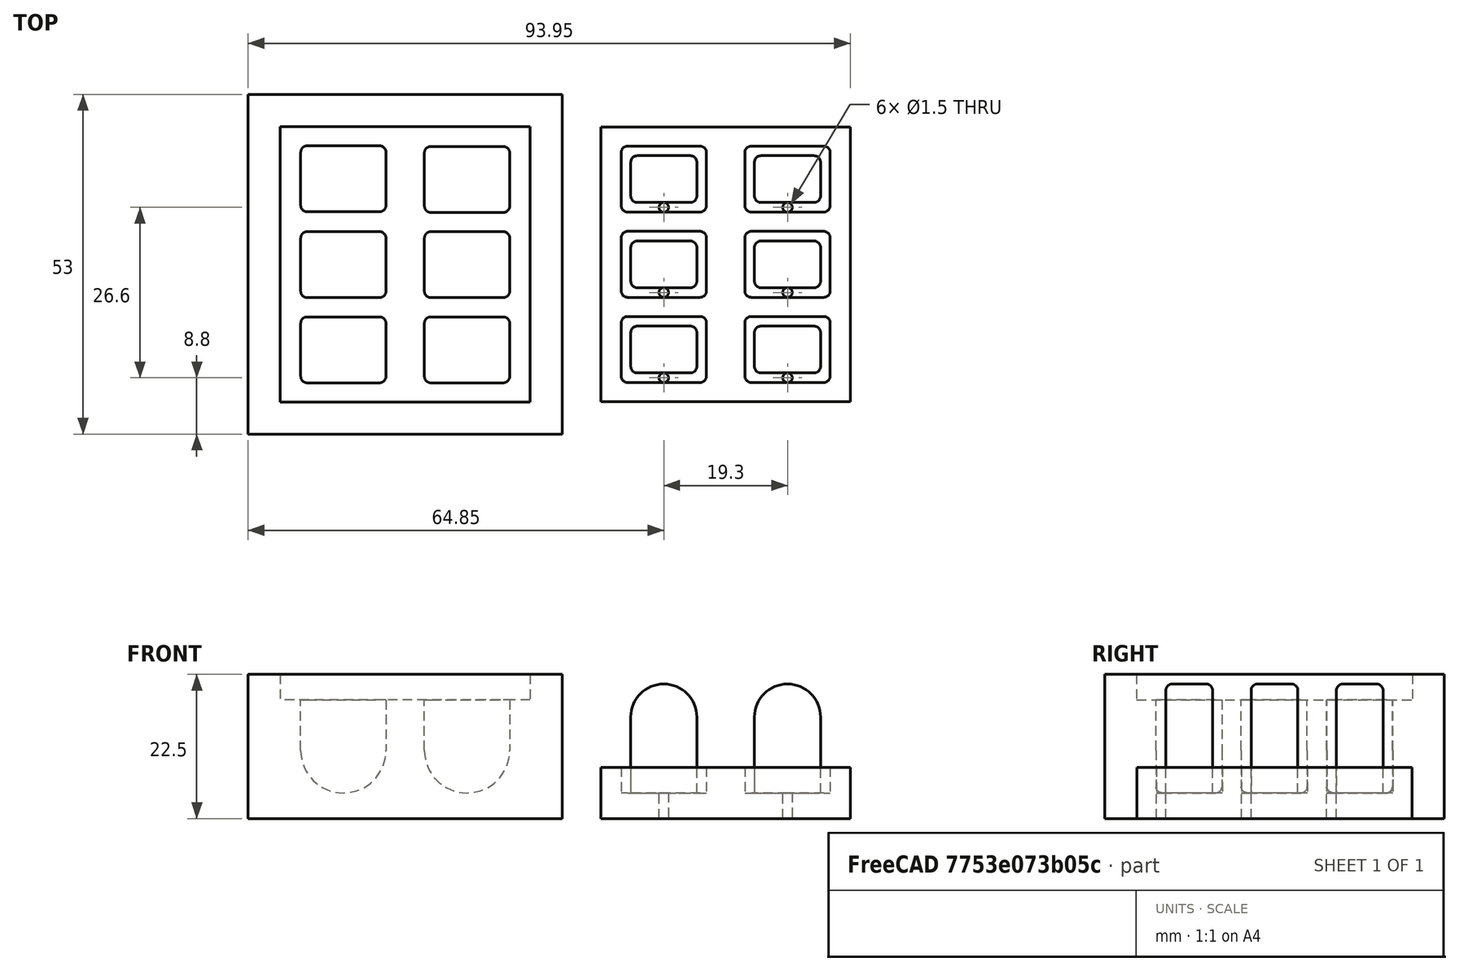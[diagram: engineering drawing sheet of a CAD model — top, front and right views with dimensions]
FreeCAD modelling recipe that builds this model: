
FCSTD DOCUMENT  (FreeCAD 0.21R33771 (Git))
Label: endcap_v3
License: All rights reserved
LicenseURL: http://en.wikipedia.org/wiki/All_rights_reserved
objects: Part::FeaturePython×12, Sketcher::SketchObject×9, Part::Cut×6, PartDesign::Pocket×5, Part::MultiFuse×5, PartDesign::Pad×4, PartDesign::Body×4, PartDesign::LinearPattern×4, Mesh::Feature×3, PartDesign::Fillet×2, Part::Fuse×1
note: 63 computed .brp shape members not serialized (recipe doc carries the construction recipe); baked Part::Feature solids carry a one-line shape summary decoded from their .brp

FEATURE [Sketcher::SketchObject] Sketch
  FullyConstrained = true
  MapMode = 5
  Support = -> [XY_Plane]
  sketch-geometry (5):
    g0: LineSegment StartX=24.5 StartY=-26.5 StartZ=0 EndX=24.5 EndY=26.5 EndZ=0
    g1: LineSegment StartX=24.5 StartY=26.5 StartZ=0 EndX=-24.5 EndY=26.5 EndZ=0
    g2: LineSegment StartX=-24.5 StartY=26.5 StartZ=0 EndX=-24.5 EndY=-26.5 EndZ=0
    g3: LineSegment StartX=-24.5 StartY=-26.5 StartZ=0 EndX=24.5 EndY=-26.5 EndZ=0
    g4: GeomPoint X=0 Y=0 Z=0
  constraints (12):
    c: Coincident(g0,g1)
    c: Coincident(g1,g2)
    c: Coincident(g2,g3)
    c: Coincident(g3,g0)
    c: Horizontal(g1)
    c: Horizontal(g3)
    c: Vertical(g0)
    c: Vertical(g2)
    c: Symmetric(g1,g0,g4)
    c: Coincident(g4,g-1)
    c: Distance(g1) = 49
    c: Distance(g2) = 53
FEATURE [PartDesign::Pad] Pad
  Direction = (0,0,1)
  Length = 22.5
  Length2 = 10
  Profile = -> Sketch
  ReferenceAxis = -> Sketch [N_Axis]
  Type = 0
  expr: Length = 14.5 + 4 + 4
FEATURE [Sketcher::SketchObject] Sketch001
  FullyConstrained = true
  MapMode = 5
  Placement = pos=(0,0,22.5) rot=(0,0,1;0rad)
  Support = -> [Pad]
  sketch-geometry (5):
    g0: LineSegment StartX=19.5 StartY=-21.5 StartZ=0 EndX=19.5 EndY=21.5 EndZ=0
    g1: LineSegment StartX=19.5 StartY=21.5 StartZ=0 EndX=-19.5 EndY=21.5 EndZ=0
    g2: LineSegment StartX=-19.5 StartY=21.5 StartZ=0 EndX=-19.5 EndY=-21.5 EndZ=0
    g3: LineSegment StartX=-19.5 StartY=-21.5 StartZ=0 EndX=19.5 EndY=-21.5 EndZ=0
    g4: GeomPoint X=0 Y=0 Z=0
  constraints (12):
    c: Coincident(g0,g1)
    c: Coincident(g1,g2)
    c: Coincident(g2,g3)
    c: Coincident(g3,g0)
    c: Horizontal(g1)
    c: Horizontal(g3)
    c: Vertical(g0)
    c: Vertical(g2)
    c: Symmetric(g1,g0,g4)
    c: Coincident(g4,g-1)
    c: Distance(g1) = 39
    c: Distance(g2) = 43
FEATURE [PartDesign::Pocket] Pocket
  BaseFeature = -> Pad
  Direction = (0,0,-1)
  Length = 4
  Length2 = 5
  Profile = -> Sketch001
  ReferenceAxis = -> Sketch001 [N_Axis]
  Type = 0
FEATURE [PartDesign::Body] Body  label="base"
  Group = -> [Sketch,Pad,Sketch001,Pocket]
  Origin = -> Origin
  Tip = -> Pocket
FEATURE [Sketcher::SketchObject] Sketch002
  FullyConstrained = true
  MapMode = 5
  Placement = pos=(0,0,0) rot=(1,0,0;1.5708rad)
  Support = -> [XZ_Plane001]
  sketch-geometry (4):
    g0: LineSegment StartX=-6.65 StartY=0 StartZ=0 EndX=6.65 EndY=0 EndZ=0
    g1: LineSegment StartX=6.65 StartY=0 StartZ=0 EndX=6.65 EndY=-7.85 EndZ=0
    g2: ArcOfCircle CenterX=-2.765e-13 CenterY=-7.85 CenterZ=0 NormalX=0 NormalY=0 NormalZ=1 AngleXU=0 Radius=6.65 StartAngle=3.14159 EndAngle=6.28319
    g3: LineSegment StartX=-6.65 StartY=-7.85 StartZ=0 EndX=-6.65 EndY=0 EndZ=0
  constraints (10):
    c: PointOnObject(g0,g-1)
    c: Coincident(g0,g1)
    c: Vertical(g1)
    c: Tangent(g1,g2) = 1.5708
    c: Tangent(g2,g3) = 1.5708
    c: Coincident(g3,g0)
    c: Diameter(g2) = 13.3
    c: Distance(g3) = 7.85
    c: Distance(g0) = 13.3
    c: Symmetric(g0,g0,g-2)
FEATURE [PartDesign::Pad] Pad001
  Direction = (0,-1,2e-16)
  Length = 10.3
  Length2 = 10
  Placement = pos=(0,0,0) rot=(1,0,0;1.5708rad)
  Profile = -> Sketch002
  ReferenceAxis = -> Sketch002 [N_Axis]
  Type = 0
FEATURE [PartDesign::Fillet] Fillet
  Base = -> Pad001 [Edge12,Edge10,Edge7,Edge11,Edge6,Edge9]
  BaseFeature = -> Pad001
  Placement = pos=(0,0,0) rot=(1,0,0;1.5708rad)
  Radius = 1
  SupportTransform = false
  UseAllEdges = false
FEATURE [PartDesign::Body] Body001  label="cup_mother"
  Group = -> [Sketch002,Pad001,Fillet]
  Origin = -> Origin001
  Placement = pos=(9.65,16.95,18.5) rot=(0,0,1;0rad)
  Tip = -> Fillet
FEATURE [Part::FeaturePython] Clone  label="cup001"  # Draft clone (typed FeaturePython)
  AttacherType = Attacher::AttachEngine3D
  Fuse = false
  Objects = -> [Body001]
  Placement = pos=(9.65,18.4,18.5) rot=(0,0,1;0rad)
  Scale = (1,1,1)
FEATURE [Part::FeaturePython] Clone001  label="cup002"  # Draft clone (typed FeaturePython)
  AttacherType = Attacher::AttachEngine3D
  Fuse = false
  Objects = -> [Clone]
  Placement = pos=(9.65,5.1,18.5) rot=(0,0,1;0rad)
  Scale = (1,1,1)
FEATURE [Part::FeaturePython] Clone002  label="cup003"  # Draft clone (typed FeaturePython)
  AttacherType = Attacher::AttachEngine3D
  Fuse = false
  Objects = -> [Clone001]
  Placement = pos=(9.65,-8.2,18.5) rot=(0,0,1;0rad)
  Scale = (1,1,1)
FEATURE [Part::FeaturePython] Clone003  label="cup004"  # Draft clone (typed FeaturePython)
  AttacherType = Attacher::AttachEngine3D
  Fuse = false
  Objects = -> [Clone002]
  Placement = pos=(-9.65,18.5,18.5) rot=(0,0,1;0rad)
  Scale = (1,1,1)
FEATURE [Part::FeaturePython] Clone004  label="cup005"  # Draft clone (typed FeaturePython)
  AttacherType = Attacher::AttachEngine3D
  Fuse = false
  Objects = -> [Clone003]
  Placement = pos=(-9.65,5.1,18.5) rot=(0,0,1;0rad)
  Scale = (1,1,1)
FEATURE [Part::FeaturePython] Clone005  label="cup006"  # Draft clone (typed FeaturePython)
  AttacherType = Attacher::AttachEngine3D
  Fuse = false
  Objects = -> [Clone004]
  Placement = pos=(-9.65,-8.2,18.5) rot=(0,0,1;0rad)
  Scale = (1,1,1)
FEATURE [Sketcher::SketchObject] Sketch003
  FullyConstrained = true
  MapMode = 5
  Support = -> [XY_Plane002]
  sketch-geometry (5):
    g0: LineSegment StartX=19.45 StartY=-21.45 StartZ=0 EndX=19.45 EndY=21.45 EndZ=0
    g1: LineSegment StartX=19.45 StartY=21.45 StartZ=0 EndX=-19.45 EndY=21.45 EndZ=0
    g2: LineSegment StartX=-19.45 StartY=21.45 StartZ=0 EndX=-19.45 EndY=-21.45 EndZ=0
    g3: LineSegment StartX=-19.45 StartY=-21.45 StartZ=0 EndX=19.45 EndY=-21.45 EndZ=0
    g4: GeomPoint X=0 Y=0 Z=0
  constraints (12):
    c: Coincident(g0,g1)
    c: Coincident(g1,g2)
    c: Coincident(g2,g3)
    c: Coincident(g3,g0)
    c: Horizontal(g1)
    c: Horizontal(g3)
    c: Vertical(g0)
    c: Vertical(g2)
    c: Symmetric(g1,g0,g4)
    c: Coincident(g4,g-1)
    c: Distance(g1) = 38.9
    c: Distance(g2) = 42.9
FEATURE [PartDesign::Pad] Pad002
  Direction = (0,0,1)
  Length = 8
  Length2 = 10
  Profile = -> Sketch003
  ReferenceAxis = -> Sketch003 [N_Axis]
  Type = 0
FEATURE [Sketcher::SketchObject] Sketch004  label="overflow001"
  FullyConstrained = true
  MapMode = 5
  Placement = pos=(0,0,8) rot=(0,0,1;0rad)
  Support = -> [Pad002]
  expr: Constraints[16] = 13.3 / 2
  expr: Constraints[20] = 10.3 / 2
  expr: Constraints[21] = 10.3 / 2
  sketch-geometry (9):
    g0: LineSegment StartX=-16.3 StartY=-9.15 StartZ=0 EndX=-16.3 EndY=-17.45 EndZ=0
    g1: LineSegment StartX=-15.3 StartY=-18.45 StartZ=0 EndX=-4 EndY=-18.45 EndZ=0
    g2: LineSegment StartX=-3 StartY=-17.45 StartZ=0 EndX=-3 EndY=-9.15 EndZ=0
    g3: LineSegment StartX=-4 StartY=-8.15 StartZ=0 EndX=-15.3 EndY=-8.15 EndZ=0
    g4: ArcOfCircle CenterX=-4 CenterY=-9.15 CenterZ=0 NormalX=0 NormalY=0 NormalZ=1 AngleXU=0 Radius=1 StartAngle=0 EndAngle=1.5708
    g5: ArcOfCircle CenterX=-15.3 CenterY=-9.15 CenterZ=0 NormalX=0 NormalY=0 NormalZ=1 AngleXU=0 Radius=1 StartAngle=1.5708 EndAngle=3.14159
    g6: ArcOfCircle CenterX=-15.3 CenterY=-17.45 CenterZ=0 NormalX=0 NormalY=0 NormalZ=1 AngleXU=0 Radius=1 StartAngle=3.14159 EndAngle=4.71239
    g7: ArcOfCircle CenterX=-4 CenterY=-17.45 CenterZ=0 NormalX=0 NormalY=0 NormalZ=1 AngleXU=0 Radius=1 StartAngle=4.71239 EndAngle=6.28319
    g8: GeomPoint X=-9.65 Y=-13.3 Z=0
  constraints (22):
    c: Horizontal(g1)
    c: Horizontal(g3)
    c: Vertical(g0)
    c: Vertical(g2)
    c: Tangent(g3,g4) = -1.5708
    c: Tangent(g2,g4) = -1.5708
    c: Tangent(g0,g5) = -1.5708
    c: Tangent(g3,g5) = -1.5708
    c: Tangent(g0,g6) = -1.5708
    c: Tangent(g1,g6) = -1.5708
    c: Tangent(g2,g7) = -1.5708
    c: Tangent(g1,g7) = -1.5708
    c: Radius(g4) = 1
    c: Radius(g7) = 1
    c: Radius(g5) = 1
    c: Radius(g6) = 1
    c: DistanceX(g8,g2) = 6.65
    c: DistanceX(g0,g8) = 6.65
    c: DistanceX(g8,g-1) = 9.65
    c: DistanceY(g8,g-1) = 13.3
    c: DistanceY(g1,g8) = 5.15
    c: DistanceY(g8,g3) = 5.15
FEATURE [PartDesign::Pocket] Pocket001  label="over_flow001"
  BaseFeature = -> Pad002
  Direction = (0,0,-1)
  Length = 4
  Length2 = 5
  Profile = -> Sketch004
  ReferenceAxis = -> Sketch004 [N_Axis]
  Type = 0
FEATURE [PartDesign::LinearPattern] LinearPattern
  BaseFeature = -> Pocket001
  Direction = -> Y_Axis002
  Length = 26.6
  Occurrences = 3
  Originals = -> [Pocket001]
FEATURE [Sketcher::SketchObject] Sketch005
  FullyConstrained = true
  MapMode = 5
  Placement = pos=(0,0,8) rot=(0,0,1;0rad)
  Support = -> [LinearPattern]
  expr: Constraints[18] = 13.3 / 2
  expr: Constraints[19] = 10.3 / 2
  sketch-geometry (9):
    g0: LineSegment StartX=4 StartY=-8.15 StartZ=0 EndX=15.3 EndY=-8.15 EndZ=0
    g1: LineSegment StartX=16.3 StartY=-9.15 StartZ=0 EndX=16.3 EndY=-17.45 EndZ=0
    g2: LineSegment StartX=15.3 StartY=-18.45 StartZ=0 EndX=4 EndY=-18.45 EndZ=0
    g3: LineSegment StartX=3 StartY=-17.45 StartZ=0 EndX=3 EndY=-9.15 EndZ=0
    g4: ArcOfCircle CenterX=4 CenterY=-9.15 CenterZ=0 NormalX=0 NormalY=0 NormalZ=1 AngleXU=0 Radius=1 StartAngle=1.5708 EndAngle=3.14159
    g5: ArcOfCircle CenterX=15.3 CenterY=-9.15 CenterZ=0 NormalX=0 NormalY=0 NormalZ=1 AngleXU=0 Radius=1 StartAngle=0 EndAngle=1.5708
    g6: ArcOfCircle CenterX=15.3 CenterY=-17.45 CenterZ=0 NormalX=0 NormalY=0 NormalZ=1 AngleXU=0 Radius=1 StartAngle=4.71239 EndAngle=6.28319
    g7: ArcOfCircle CenterX=4 CenterY=-17.45 CenterZ=0 NormalX=0 NormalY=0 NormalZ=1 AngleXU=0 Radius=1 StartAngle=3.14159 EndAngle=4.71239
    g8: GeomPoint X=9.65 Y=-13.3 Z=0
  constraints (22):
    c: Horizontal(g0)
    c: Horizontal(g2)
    c: Vertical(g1)
    c: Vertical(g3)
    c: Tangent(g3,g4) = 1.5708
    c: Tangent(g0,g4) = 1.5708
    c: Tangent(g0,g5) = 1.5708
    c: Tangent(g1,g5) = 1.5708
    c: Tangent(g1,g6) = 1.5708
    c: Tangent(g2,g6) = 1.5708
    c: Tangent(g2,g7) = 1.5708
    c: Tangent(g3,g7) = 1.5708
    c: Radius(g5) = 1
    c: Radius(g4) = 1
    c: Radius(g7) = 1
    c: Radius(g6) = 1
    c: DistanceY(g2,g0) = 10.3
    c: DistanceX(g3,g1) = 13.3
    c: DistanceX(g3,g8) = 6.65
    c: DistanceY(g2,g8) = 5.15
    c: DistanceY(g8,g-1) = 13.3
    c: DistanceX(g-1,g8) = 9.65
FEATURE [PartDesign::Pocket] Pocket002  label="over_flow_cup"
  BaseFeature = -> LinearPattern
  Direction = (0,0,-1)
  Length = 4
  Length2 = 5
  Profile = -> Sketch005
  ReferenceAxis = -> Sketch005 [N_Axis]
  Type = 0
FEATURE [PartDesign::LinearPattern] LinearPattern001
  BaseFeature = -> Pocket002
  Direction = -> Y_Axis002
  Length = 26.6
  Occurrences = 3
  Originals = -> [Pocket002]
FEATURE [Sketcher::SketchObject] Sketch006
  FullyConstrained = true
  MapMode = 5
  Placement = pos=(0,0,0) rot=(1,0,0;1.5708rad)
  Support = -> [XZ_Plane003]
  sketch-geometry (4):
    g0: LineSegment StartX=5.15 StartY=0 StartZ=0 EndX=5.15 EndY=11.85 EndZ=0
    g1: ArcOfCircle CenterX=0 CenterY=11.85 CenterZ=0 NormalX=0 NormalY=0 NormalZ=1 AngleXU=0 Radius=5.15 StartAngle=1e-16 EndAngle=3.14159
    g2: LineSegment StartX=-5.15 StartY=11.85 StartZ=0 EndX=-5.15 EndY=0 EndZ=0
    g3: LineSegment StartX=-5.15 StartY=0 StartZ=0 EndX=5.15 EndY=0 EndZ=0
  constraints (12):
    c: PointOnObject(g0,g-1)
    c: Vertical(g0)
    c: Tangent(g0,g1) = -1.5708
    c: Coincident(g1,g2)
    c: Vertical(g2)
    c: Coincident(g2,g3)
    c: Coincident(g3,g0)
    c: Horizontal(g3)
    c: Diameter(g1) = 10.3
    c: Distance(g2) = 11.85
    c: PointOnObject(g1,g-2)
    c: Horizontal(g1,g1)
FEATURE [PartDesign::Pad] Pad003
  Direction = (0,-1,2e-16)
  Length = 7.3
  Length2 = 10
  Placement = pos=(0,0,0) rot=(1,0,0;1.5708rad)
  Profile = -> Sketch006
  ReferenceAxis = -> Sketch006 [N_Axis]
  Type = 0
FEATURE [PartDesign::Fillet] Fillet001
  Base = -> Pad003 [Edge10,Edge7,Edge4,Edge3,Edge6,Edge9]
  BaseFeature = -> Pad003
  Placement = pos=(0,0,0) rot=(1,0,0;1.5708rad)
  Radius = 1
  SupportTransform = false
  UseAllEdges = false
FEATURE [PartDesign::Body] Body003  label="finger_mother"
  Group = -> [Sketch006,Pad003,Fillet001]
  Origin = -> Origin003
  Placement = pos=(9.65,16.95,4) rot=(0,0,1;0rad)
  Tip = -> Fillet001
FEATURE [Part::FeaturePython] Clone006  label="finger001"  # Draft clone (typed FeaturePython)
  AttacherType = Attacher::AttachEngine3D
  Fuse = false
  Objects = -> [Body003]
  Placement = pos=(9.65,3.65,4) rot=(0,0,1;0rad)
  Scale = (1,1,1)
FEATURE [Part::FeaturePython] Clone007  label="finger002"  # Draft clone (typed FeaturePython)
  AttacherType = Attacher::AttachEngine3D
  Fuse = false
  Objects = -> [Clone006]
  Placement = pos=(9.65,-9.65,4) rot=(0,0,1;0rad)
  Scale = (1,1,1)
FEATURE [Part::FeaturePython] Clone008  label="finger003"  # Draft clone (typed FeaturePython)
  AttacherType = Attacher::AttachEngine3D
  Fuse = false
  Objects = -> [Clone007]
  Placement = pos=(-9.65,16.95,4) rot=(0,0,1;0rad)
  Scale = (1,1,1)
FEATURE [Part::FeaturePython] Clone009  label="finger004"  # Draft clone (typed FeaturePython)
  AttacherType = Attacher::AttachEngine3D
  Fuse = false
  Objects = -> [Clone008]
  Placement = pos=(-9.65,3.65,4) rot=(0,0,1;0rad)
  Scale = (1,1,1)
FEATURE [Part::FeaturePython] Clone010  label="finger005"  # Draft clone (typed FeaturePython)
  AttacherType = Attacher::AttachEngine3D
  Fuse = false
  Objects = -> [Clone009]
  Placement = pos=(-9.65,-9.65,4) rot=(0,0,1;0rad)
  Scale = (1,1,1)
FEATURE [Part::FeaturePython] Clone011  label="finger006"  # Draft clone (typed FeaturePython)
  AttacherType = Attacher::AttachEngine3D
  Fuse = false
  Objects = -> [Clone010]
  Placement = pos=(9.65,16.95,4) rot=(0,0,1;0rad)
  Scale = (1,1,1)
FEATURE [Part::Cut] Cut
  Base = -> Body
  Tool = -> Clone
FEATURE [Part::Cut] Cut001
  Base = -> Cut
  Tool = -> Clone001
FEATURE [Part::Cut] Cut002
  Base = -> Cut001
  Tool = -> Clone002
FEATURE [Part::Cut] Cut003
  Base = -> Cut002
  Tool = -> Clone003
FEATURE [Part::Cut] Cut004
  Base = -> Cut003
  Tool = -> Clone004
FEATURE [Part::Cut] Cut005  label="mold_bottom"
  Base = -> Cut004
  Tool = -> Clone005
FEATURE [Sketcher::SketchObject] Sketch007  label="breathing_hole001"
  FullyConstrained = true
  MapMode = 5
  Placement = pos=(0,0,4) rot=(0,0,1;0rad)
  Support = -> [Pocket002]
  sketch-geometry (1):
    g0: Circle CenterX=-9.65 CenterY=-17.7 CenterZ=0 NormalX=0 NormalY=0 NormalZ=1 AngleXU=0 Radius=0.75
  constraints (3):
    c: Diameter(g0) = 1.5
    c: DistanceY(g0,g-1) = 17.7
    c: DistanceX(g0,g-1) = 9.65
FEATURE [PartDesign::Pocket] Pocket003  label="breathing_hole_cut000"
  BaseFeature = -> LinearPattern001
  Direction = (0,0,-1)
  Length = 5
  Length2 = 5
  Profile = -> Sketch007
  ReferenceAxis = -> Sketch007 [N_Axis]
  Type = 0
FEATURE [PartDesign::LinearPattern] LinearPattern002
  BaseFeature = -> Pocket003
  Direction = -> Y_Axis002
  Length = 26.6
  Occurrences = 3
  Originals = -> [Pocket003]
FEATURE [Sketcher::SketchObject] Sketch008  label="breathing_hole_002"
  FullyConstrained = true
  MapMode = 5
  Placement = pos=(0,0,4) rot=(0,0,1;0rad)
  Support = -> [LinearPattern002]
  sketch-geometry (1):
    g0: Circle CenterX=9.65 CenterY=-17.7 CenterZ=0 NormalX=0 NormalY=0 NormalZ=1 AngleXU=0 Radius=0.75
  constraints (3):
    c: Diameter(g0) = 1.5
    c: DistanceY(g0,g-1) = 17.7
    c: DistanceX(g-1,g0) = 9.65
FEATURE [PartDesign::Pocket] Pocket004  label="breathing_hole_cut001"
  BaseFeature = -> LinearPattern002
  Direction = (0,0,-1)
  Length = 5
  Length2 = 5
  Profile = -> Sketch008
  ReferenceAxis = -> Sketch008 [N_Axis]
  Type = 0
FEATURE [PartDesign::LinearPattern] LinearPattern003
  BaseFeature = -> Pocket004
  Direction = -> Y_Axis002
  Length = 26.6
  Occurrences = 3
  Originals = -> [Pocket004]
FEATURE [PartDesign::Body] Body002  label="top"
  Group = -> [Sketch003,Pad002,Sketch004,Pocket001,LinearPattern,Sketch005,Pocket002,LinearPattern001,Sketch007,Pocket003,LinearPattern002,Sketch008,Pocket004,LinearPattern003]
  Origin = -> Origin002
  Tip = -> LinearPattern003
FEATURE [Part::Fuse] Fusion
  Base = -> Body002
  Tool = -> Clone011
FEATURE [Part::MultiFuse] Fusion001
  Shapes = -> [Fusion,Clone006]
FEATURE [Part::MultiFuse] Fusion002
  Shapes = -> [Fusion001,Clone007]
FEATURE [Part::MultiFuse] Fusion003
  Shapes = -> [Fusion002,Clone008]
FEATURE [Part::MultiFuse] Fusion004
  Shapes = -> [Fusion003,Clone009]
FEATURE [Part::MultiFuse] Fusion005  label="mold_top"
  Placement = pos=(50,0,0) rot=(0,1,0;0rad)
  Shapes = -> [Fusion004,Clone010]
FEATURE [Mesh::Feature] Mesh001  label="mold_bottom (Meshed)"
FEATURE [Mesh::Feature] Mesh  label="mold_top (Meshed)"
FEATURE [Mesh::Feature] Mesh002  label="mold_top (Meshed)001"
